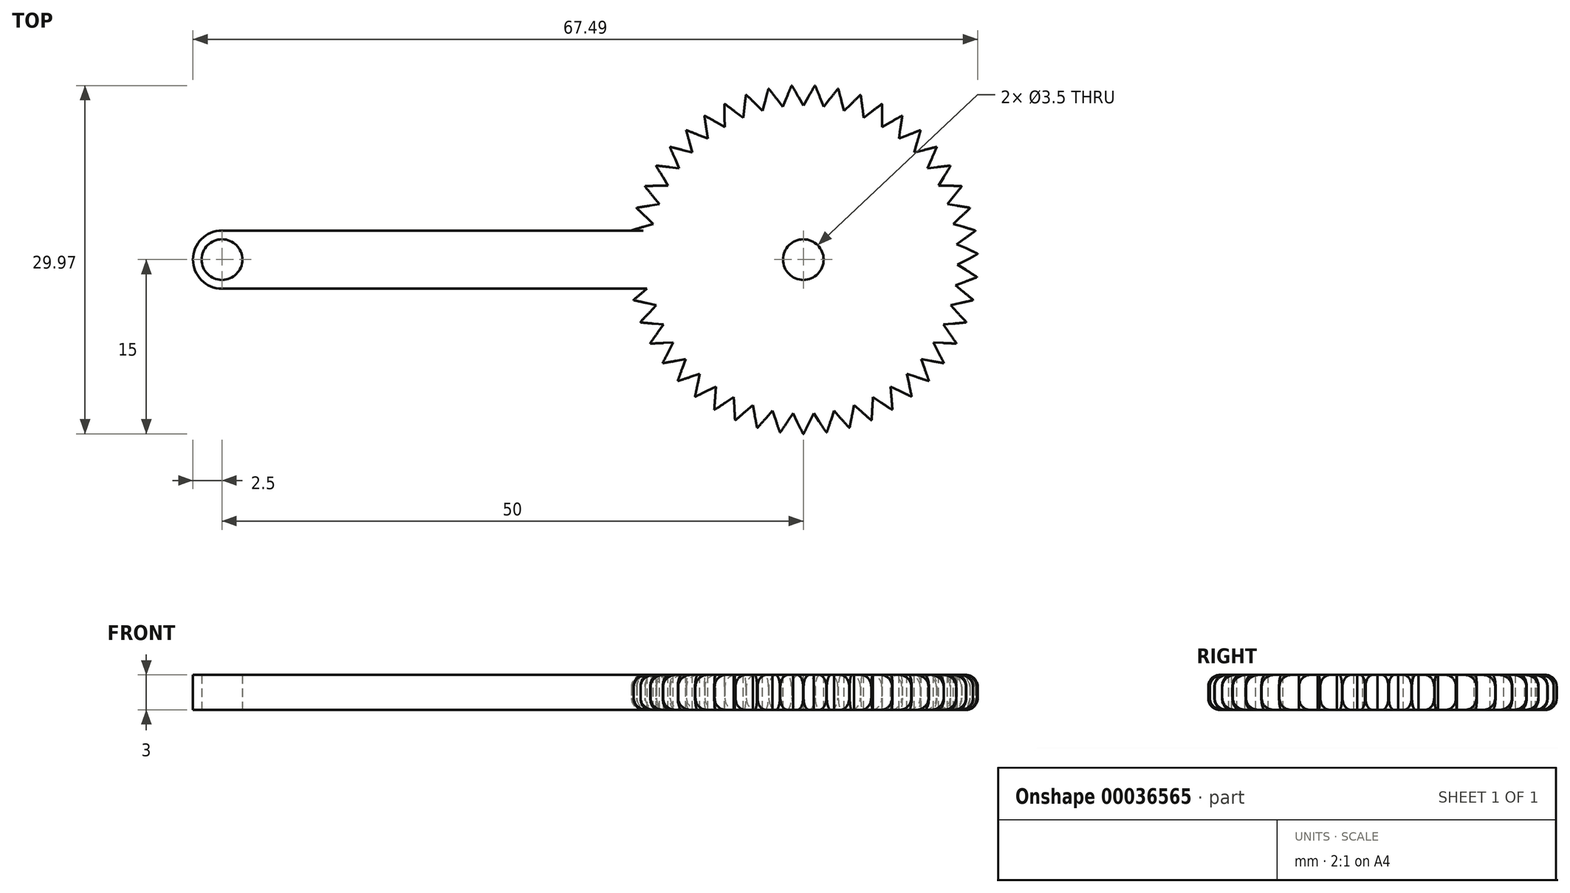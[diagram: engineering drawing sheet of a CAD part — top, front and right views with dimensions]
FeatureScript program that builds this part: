
annotation { "Feature Type Name" : "Feature", "Feature Type Description" : "" }
export const myFeature = defineFeature(function(context is Context, id is Id, definition is map)
    precondition{}
    {
        {
            var Q0;
            Q0=qCreatedBy(makeId("Top.planeOp"),FACE);
            var sketch = newSketch(context, id + "F0", { "sketchPlane" : qUnion([Q0])});
            skCircle(sketch, "E0", {"center": v(0, 0) * mm, "radius": 15 * mm});
            skSolve(sketch);
        }
        {
            var Q0;
            Q0 = qSketchRegion(id + "F0", true);
            extrude(context, id + "F1", {"entities" : qUnion([Q0]), "depth" : 3 * mm});
        }
        {
            var Q0;
            Q0=makeQuery(id+"F1.opExtrude","CAP_FACE",FACE,{"disambiguationData":[OSD([sQuery(id+"F0.wireOp",EDGE,"E0")])],"isStart":false});
            var Q1;
            Q1=makeQuery(id+"F1.opExtrude","CAP_EDGE",EDGE,{"disambiguationData":[OSD([sQuery(id+"F0.wireOp",EDGE,"E0")])],"isStart":true});
            fillet(context, id + "F2", {"entities" : qUnion([Q0, Q1]), "radius" : 1 * mm, "tangentPropagation" : true, "allowEdgeOverflow" : false});
        }
        {
            var Q0;
            Q0=makeQuery(id+"F1.opExtrude","CAP_FACE",FACE,{"disambiguationData":[OSD([sQuery(id+"F0.wireOp",EDGE,"E0")])],"isStart":false});
            var sketch = newSketch(context, id + "F3", { "sketchPlane" : qUnion([Q0])});
            skCircle(sketch, "E1.cCircle", {"center": v(0, 14.42) * mm, "radius": 0.58 * mm, "construction": true});
            skLineSegment(sketch, "E1.0", {"start": v(-1, 15) * mm, "end": v(1, 15) * mm});
            skLineSegment(sketch, "E1.1", {"start": v(1, 15) * mm, "end": v(0, 13.27) * mm});
            skLineSegment(sketch, "E1.2", {"start": v(0, 13.27) * mm, "end": v(-1, 15) * mm});
            skPoint(sketch, "E1.0.midPoint", {"position": v(0, 15) * mm});
            skLineSegment(sketch, "E2.1.0", {"start": v(-1, 15) * mm, "end": v(-1.77, 13.15) * mm});
            skLineSegment(sketch, "E2.1.1", {"start": v(-1.77, 13.15) * mm, "end": v(-3, 14.73) * mm});
            skLineSegment(sketch, "E2.1.2", {"start": v(-3, 14.73) * mm, "end": v(-1, 15) * mm});
            skLineSegment(sketch, "E2.2.0", {"start": v(-3, 14.73) * mm, "end": v(-3.5, 12.8) * mm});
            skLineSegment(sketch, "E2.2.1", {"start": v(-3.5, 12.8) * mm, "end": v(-4.93, 14.2) * mm});
            skLineSegment(sketch, "E2.2.2", {"start": v(-4.93, 14.2) * mm, "end": v(-3, 14.73) * mm});
            skLineSegment(sketch, "E2.3.0", {"start": v(-4.94, 14.2) * mm, "end": v(-5.18, 12.22) * mm});
            skLineSegment(sketch, "E2.3.1", {"start": v(-5.18, 12.22) * mm, "end": v(-6.78, 13.42) * mm});
            skLineSegment(sketch, "E2.3.2", {"start": v(-6.78, 13.42) * mm, "end": v(-4.94, 14.2) * mm});
            skLineSegment(sketch, "E2.4.0", {"start": v(-6.78, 13.42) * mm, "end": v(-6.76, 11.42) * mm});
            skLineSegment(sketch, "E2.4.1", {"start": v(-6.76, 11.42) * mm, "end": v(-8.5, 12.4) * mm});
            skLineSegment(sketch, "E2.4.2", {"start": v(-8.5, 12.4) * mm, "end": v(-6.78, 13.42) * mm});
            skLineSegment(sketch, "E2.5.0", {"start": v(-8.51, 12.4) * mm, "end": v(-8.22, 10.41) * mm});
            skLineSegment(sketch, "E2.5.1", {"start": v(-8.22, 10.41) * mm, "end": v(-10.08, 11.15) * mm});
            skLineSegment(sketch, "E2.5.2", {"start": v(-10.08, 11.15) * mm, "end": v(-8.51, 12.4) * mm});
            skLineSegment(sketch, "E2.6.0", {"start": v(-10.09, 11.15) * mm, "end": v(-9.54, 9.22) * mm});
            skLineSegment(sketch, "E2.6.1", {"start": v(-9.54, 9.22) * mm, "end": v(-11.48, 9.7) * mm});
            skLineSegment(sketch, "E2.6.2", {"start": v(-11.48, 9.7) * mm, "end": v(-10.09, 11.15) * mm});
            skLineSegment(sketch, "E2.7.0", {"start": v(-11.48, 9.7) * mm, "end": v(-10.68, 7.87) * mm});
            skLineSegment(sketch, "E2.7.1", {"start": v(-10.68, 7.87) * mm, "end": v(-12.67, 8.1) * mm});
            skLineSegment(sketch, "E2.7.2", {"start": v(-12.67, 8.1) * mm, "end": v(-11.48, 9.7) * mm});
            skLineSegment(sketch, "E2.8.0", {"start": v(-12.67, 8.09) * mm, "end": v(-11.64, 6.38) * mm});
            skLineSegment(sketch, "E2.8.1", {"start": v(-11.64, 6.38) * mm, "end": v(-13.63, 6.33) * mm});
            skLineSegment(sketch, "E2.8.2", {"start": v(-13.63, 6.33) * mm, "end": v(-12.67, 8.09) * mm});
            skLineSegment(sketch, "E2.9.0", {"start": v(-13.64, 6.32) * mm, "end": v(-12.38, 4.77) * mm});
            skLineSegment(sketch, "E2.9.1", {"start": v(-12.38, 4.77) * mm, "end": v(-14.36, 4.46) * mm});
            skLineSegment(sketch, "E2.9.2", {"start": v(-14.36, 4.46) * mm, "end": v(-13.64, 6.32) * mm});
            skLineSegment(sketch, "E2.10.0", {"start": v(-14.36, 4.45) * mm, "end": v(-12.9, 3.08) * mm});
            skLineSegment(sketch, "E2.10.1", {"start": v(-12.9, 3.08) * mm, "end": v(-14.82, 2.5) * mm});
            skLineSegment(sketch, "E2.10.2", {"start": v(-14.82, 2.5) * mm, "end": v(-14.36, 4.45) * mm});
            skLineSegment(sketch, "E2.11.0", {"start": v(-14.82, 2.5) * mm, "end": v(-13.2, 1.33) * mm});
            skLineSegment(sketch, "E2.11.1", {"start": v(-13.2, 1.33) * mm, "end": v(-15.02, 0.5) * mm});
            skLineSegment(sketch, "E2.11.2", {"start": v(-15.02, 0.5) * mm, "end": v(-14.82, 2.5) * mm});
            skLineSegment(sketch, "E2.12.0", {"start": v(-15.03, 0.5) * mm, "end": v(-13.26, -0.44) * mm});
            skLineSegment(sketch, "E2.12.1", {"start": v(-13.26, -0.44) * mm, "end": v(-14.96, -1.5) * mm});
            skLineSegment(sketch, "E2.12.2", {"start": v(-14.96, -1.5) * mm, "end": v(-15.03, 0.5) * mm});
            skLineSegment(sketch, "E2.13.0", {"start": v(-14.96, -1.5) * mm, "end": v(-13.08, -2.2) * mm});
            skLineSegment(sketch, "E2.13.1", {"start": v(-13.08, -2.2) * mm, "end": v(-14.62, -3.48) * mm});
            skLineSegment(sketch, "E2.13.2", {"start": v(-14.62, -3.48) * mm, "end": v(-14.96, -1.5) * mm});
            skLineSegment(sketch, "E2.14.0", {"start": v(-14.62, -3.49) * mm, "end": v(-12.67, -3.93) * mm});
            skLineSegment(sketch, "E2.14.1", {"start": v(-12.67, -3.93) * mm, "end": v(-14.03, -5.4) * mm});
            skLineSegment(sketch, "E2.14.2", {"start": v(-14.03, -5.4) * mm, "end": v(-14.62, -3.49) * mm});
            skLineSegment(sketch, "E2.15.0", {"start": v(-14.03, -5.4) * mm, "end": v(-12.04, -5.58) * mm});
            skLineSegment(sketch, "E2.15.1", {"start": v(-12.04, -5.58) * mm, "end": v(-13.19, -7.22) * mm});
            skLineSegment(sketch, "E2.15.2", {"start": v(-13.19, -7.22) * mm, "end": v(-14.03, -5.4) * mm});
            skLineSegment(sketch, "E2.16.0", {"start": v(-13.18, -7.23) * mm, "end": v(-11.18, -7.14) * mm});
            skLineSegment(sketch, "E2.16.1", {"start": v(-11.18, -7.14) * mm, "end": v(-12.1, -8.91) * mm});
            skLineSegment(sketch, "E2.16.2", {"start": v(-12.1, -8.91) * mm, "end": v(-13.18, -7.23) * mm});
            skLineSegment(sketch, "E2.17.0", {"start": v(-12.1, -8.92) * mm, "end": v(-10.13, -8.57) * mm});
            skLineSegment(sketch, "E2.17.1", {"start": v(-10.13, -8.57) * mm, "end": v(-10.8, -10.45) * mm});
            skLineSegment(sketch, "E2.17.2", {"start": v(-10.8, -10.45) * mm, "end": v(-12.1, -8.92) * mm});
            skLineSegment(sketch, "E2.18.0", {"start": v(-10.8, -10.45) * mm, "end": v(-8.9, -9.84) * mm});
            skLineSegment(sketch, "E2.18.1", {"start": v(-8.9, -9.84) * mm, "end": v(-9.32, -11.8) * mm});
            skLineSegment(sketch, "E2.18.2", {"start": v(-9.32, -11.8) * mm, "end": v(-10.8, -10.45) * mm});
            skLineSegment(sketch, "E2.19.0", {"start": v(-9.31, -11.8) * mm, "end": v(-7.5, -10.94) * mm});
            skLineSegment(sketch, "E2.19.1", {"start": v(-7.5, -10.94) * mm, "end": v(-7.66, -12.93) * mm});
            skLineSegment(sketch, "E2.19.2", {"start": v(-7.66, -12.93) * mm, "end": v(-9.31, -11.8) * mm});
            skLineSegment(sketch, "E2.20.0", {"start": v(-7.66, -12.94) * mm, "end": v(-5.98, -11.84) * mm});
            skLineSegment(sketch, "E2.20.1", {"start": v(-5.98, -11.84) * mm, "end": v(-5.87, -13.84) * mm});
            skLineSegment(sketch, "E2.20.2", {"start": v(-5.87, -13.84) * mm, "end": v(-7.66, -12.94) * mm});
            skLineSegment(sketch, "E2.21.0", {"start": v(-5.87, -13.84) * mm, "end": v(-4.35, -12.53) * mm});
            skLineSegment(sketch, "E2.21.1", {"start": v(-4.35, -12.53) * mm, "end": v(-3.98, -14.5) * mm});
            skLineSegment(sketch, "E2.21.2", {"start": v(-3.98, -14.5) * mm, "end": v(-5.87, -13.84) * mm});
            skLineSegment(sketch, "E2.22.0", {"start": v(-3.97, -14.5) * mm, "end": v(-2.64, -13) * mm});
            skLineSegment(sketch, "E2.22.1", {"start": v(-2.64, -13) * mm, "end": v(-2, -14.9) * mm});
            skLineSegment(sketch, "E2.22.2", {"start": v(-2, -14.9) * mm, "end": v(-3.97, -14.5) * mm});
            skLineSegment(sketch, "E2.23.0", {"start": v(-2, -14.9) * mm, "end": v(-0.89, -13.24) * mm});
            skLineSegment(sketch, "E2.23.1", {"start": v(-0.89, -13.24) * mm, "end": v(0, -15.03) * mm});
            skLineSegment(sketch, "E2.23.2", {"start": v(0, -15.03) * mm, "end": v(-2, -14.9) * mm});
            skLineSegment(sketch, "E2.24.0", {"start": v(0, -15.03) * mm, "end": v(0.89, -13.24) * mm});
            skLineSegment(sketch, "E2.24.1", {"start": v(0.89, -13.24) * mm, "end": v(2, -14.9) * mm});
            skLineSegment(sketch, "E2.24.2", {"start": v(2, -14.9) * mm, "end": v(0, -15.03) * mm});
            skLineSegment(sketch, "E2.25.0", {"start": v(2, -14.9) * mm, "end": v(2.64, -13) * mm});
            skLineSegment(sketch, "E2.25.1", {"start": v(2.64, -13) * mm, "end": v(3.97, -14.5) * mm});
            skLineSegment(sketch, "E2.25.2", {"start": v(3.97, -14.5) * mm, "end": v(2, -14.9) * mm});
            skLineSegment(sketch, "E2.26.0", {"start": v(3.98, -14.5) * mm, "end": v(4.35, -12.53) * mm});
            skLineSegment(sketch, "E2.26.1", {"start": v(4.35, -12.53) * mm, "end": v(5.87, -13.84) * mm});
            skLineSegment(sketch, "E2.26.2", {"start": v(5.87, -13.84) * mm, "end": v(3.98, -14.5) * mm});
            skLineSegment(sketch, "E2.27.0", {"start": v(5.87, -13.84) * mm, "end": v(5.98, -11.84) * mm});
            skLineSegment(sketch, "E2.27.1", {"start": v(5.98, -11.84) * mm, "end": v(7.66, -12.94) * mm});
            skLineSegment(sketch, "E2.27.2", {"start": v(7.66, -12.94) * mm, "end": v(5.87, -13.84) * mm});
            skLineSegment(sketch, "E2.28.0", {"start": v(7.66, -12.93) * mm, "end": v(7.5, -10.94) * mm});
            skLineSegment(sketch, "E2.28.1", {"start": v(7.5, -10.94) * mm, "end": v(9.31, -11.8) * mm});
            skLineSegment(sketch, "E2.28.2", {"start": v(9.31, -11.8) * mm, "end": v(7.66, -12.93) * mm});
            skLineSegment(sketch, "E2.29.0", {"start": v(9.32, -11.8) * mm, "end": v(8.9, -9.84) * mm});
            skLineSegment(sketch, "E2.29.1", {"start": v(8.9, -9.84) * mm, "end": v(10.8, -10.45) * mm});
            skLineSegment(sketch, "E2.29.2", {"start": v(10.8, -10.45) * mm, "end": v(9.32, -11.8) * mm});
            skLineSegment(sketch, "E2.30.0", {"start": v(10.8, -10.45) * mm, "end": v(10.13, -8.57) * mm});
            skLineSegment(sketch, "E2.30.1", {"start": v(10.13, -8.57) * mm, "end": v(12.1, -8.92) * mm});
            skLineSegment(sketch, "E2.30.2", {"start": v(12.1, -8.92) * mm, "end": v(10.8, -10.45) * mm});
            skLineSegment(sketch, "E2.31.0", {"start": v(12.1, -8.91) * mm, "end": v(11.18, -7.14) * mm});
            skLineSegment(sketch, "E2.31.1", {"start": v(11.18, -7.14) * mm, "end": v(13.18, -7.23) * mm});
            skLineSegment(sketch, "E2.31.2", {"start": v(13.18, -7.23) * mm, "end": v(12.1, -8.91) * mm});
            skLineSegment(sketch, "E2.32.0", {"start": v(13.19, -7.22) * mm, "end": v(12.04, -5.58) * mm});
            skLineSegment(sketch, "E2.32.1", {"start": v(12.04, -5.58) * mm, "end": v(14.03, -5.4) * mm});
            skLineSegment(sketch, "E2.32.2", {"start": v(14.03, -5.4) * mm, "end": v(13.19, -7.22) * mm});
            skLineSegment(sketch, "E2.33.0", {"start": v(14.03, -5.4) * mm, "end": v(12.67, -3.93) * mm});
            skLineSegment(sketch, "E2.33.1", {"start": v(12.67, -3.93) * mm, "end": v(14.62, -3.49) * mm});
            skLineSegment(sketch, "E2.33.2", {"start": v(14.62, -3.49) * mm, "end": v(14.03, -5.4) * mm});
            skLineSegment(sketch, "E2.34.0", {"start": v(14.62, -3.48) * mm, "end": v(13.08, -2.2) * mm});
            skLineSegment(sketch, "E2.34.1", {"start": v(13.08, -2.2) * mm, "end": v(14.96, -1.5) * mm});
            skLineSegment(sketch, "E2.34.2", {"start": v(14.96, -1.5) * mm, "end": v(14.62, -3.48) * mm});
            skLineSegment(sketch, "E2.35.0", {"start": v(14.96, -1.5) * mm, "end": v(13.26, -0.44) * mm});
            skLineSegment(sketch, "E2.35.1", {"start": v(13.26, -0.44) * mm, "end": v(15.03, 0.5) * mm});
            skLineSegment(sketch, "E2.35.2", {"start": v(15.03, 0.5) * mm, "end": v(14.96, -1.5) * mm});
            skLineSegment(sketch, "E2.36.0", {"start": v(15.02, 0.5) * mm, "end": v(13.2, 1.33) * mm});
            skLineSegment(sketch, "E2.36.1", {"start": v(13.2, 1.33) * mm, "end": v(14.82, 2.5) * mm});
            skLineSegment(sketch, "E2.36.2", {"start": v(14.82, 2.5) * mm, "end": v(15.02, 0.5) * mm});
            skLineSegment(sketch, "E2.37.0", {"start": v(14.82, 2.5) * mm, "end": v(12.9, 3.08) * mm});
            skLineSegment(sketch, "E2.37.1", {"start": v(12.9, 3.08) * mm, "end": v(14.36, 4.45) * mm});
            skLineSegment(sketch, "E2.37.2", {"start": v(14.36, 4.45) * mm, "end": v(14.82, 2.5) * mm});
            skLineSegment(sketch, "E2.38.0", {"start": v(14.36, 4.46) * mm, "end": v(12.38, 4.77) * mm});
            skLineSegment(sketch, "E2.38.1", {"start": v(12.38, 4.77) * mm, "end": v(13.64, 6.32) * mm});
            skLineSegment(sketch, "E2.38.2", {"start": v(13.64, 6.32) * mm, "end": v(14.36, 4.46) * mm});
            skLineSegment(sketch, "E2.39.0", {"start": v(13.63, 6.33) * mm, "end": v(11.64, 6.38) * mm});
            skLineSegment(sketch, "E2.39.1", {"start": v(11.64, 6.38) * mm, "end": v(12.67, 8.09) * mm});
            skLineSegment(sketch, "E2.39.2", {"start": v(12.67, 8.09) * mm, "end": v(13.63, 6.33) * mm});
            skLineSegment(sketch, "E2.40.0", {"start": v(12.67, 8.1) * mm, "end": v(10.68, 7.87) * mm});
            skLineSegment(sketch, "E2.40.1", {"start": v(10.68, 7.87) * mm, "end": v(11.48, 9.7) * mm});
            skLineSegment(sketch, "E2.40.2", {"start": v(11.48, 9.7) * mm, "end": v(12.67, 8.1) * mm});
            skLineSegment(sketch, "E2.41.0", {"start": v(11.48, 9.7) * mm, "end": v(9.54, 9.22) * mm});
            skLineSegment(sketch, "E2.41.1", {"start": v(9.54, 9.22) * mm, "end": v(10.09, 11.15) * mm});
            skLineSegment(sketch, "E2.41.2", {"start": v(10.09, 11.15) * mm, "end": v(11.48, 9.7) * mm});
            skLineSegment(sketch, "E2.42.0", {"start": v(10.08, 11.15) * mm, "end": v(8.22, 10.41) * mm});
            skLineSegment(sketch, "E2.42.1", {"start": v(8.22, 10.41) * mm, "end": v(8.51, 12.4) * mm});
            skLineSegment(sketch, "E2.42.2", {"start": v(8.51, 12.4) * mm, "end": v(10.08, 11.15) * mm});
            skLineSegment(sketch, "E2.43.0", {"start": v(8.5, 12.4) * mm, "end": v(6.76, 11.42) * mm});
            skLineSegment(sketch, "E2.43.1", {"start": v(6.76, 11.42) * mm, "end": v(6.78, 13.42) * mm});
            skLineSegment(sketch, "E2.43.2", {"start": v(6.78, 13.42) * mm, "end": v(8.5, 12.4) * mm});
            skLineSegment(sketch, "E2.44.0", {"start": v(6.78, 13.42) * mm, "end": v(5.18, 12.22) * mm});
            skLineSegment(sketch, "E2.44.1", {"start": v(5.18, 12.22) * mm, "end": v(4.94, 14.2) * mm});
            skLineSegment(sketch, "E2.44.2", {"start": v(4.94, 14.2) * mm, "end": v(6.78, 13.42) * mm});
            skLineSegment(sketch, "E2.45.0", {"start": v(4.93, 14.2) * mm, "end": v(3.5, 12.8) * mm});
            skLineSegment(sketch, "E2.45.1", {"start": v(3.5, 12.8) * mm, "end": v(3, 14.73) * mm});
            skLineSegment(sketch, "E2.45.2", {"start": v(3, 14.73) * mm, "end": v(4.93, 14.2) * mm});
            skLineSegment(sketch, "E2.46.0", {"start": v(3, 14.73) * mm, "end": v(1.77, 13.15) * mm});
            skLineSegment(sketch, "E2.46.1", {"start": v(1.77, 13.15) * mm, "end": v(1, 15) * mm});
            skLineSegment(sketch, "E2.46.2", {"start": v(1, 15) * mm, "end": v(3, 14.73) * mm});
            skPoint(sketch, "E2.center", {"position": v(0, 0) * mm});
            skSolve(sketch);
        }
        {
            var Q0;
            Q0 = qSketchRegion(id + "F3", true);
            extrude(context, id + "F4", {"entities" : qUnion([Q0]), "operationType" : NewBodyOperationType.REMOVE, "endBound" : BoundingType.THROUGH_ALL, "oppositeDirection" : true, "depth" : 25 * mm});
        }
        {
            var Q0;
            Q0=qCreatedBy(makeId("Top.planeOp"),FACE);
            var sketch = newSketch(context, id + "F5", { "sketchPlane" : qUnion([Q0])});
            skLineSegment(sketch, "E3.bottom", {"start": v(-50, 2.5) * mm, "end": v(0, 2.5) * mm});
            skLineSegment(sketch, "E3.top", {"start": v(-50, -2.5) * mm, "end": v(0, -2.5) * mm});
            skLineSegment(sketch, "E3.right", {"start": v(0, 2.5) * mm, "end": v(0, -2.5) * mm});
            skArc(sketch, "E4", {"start": v(-50, 2.5) * mm, "mid": v(-52.5, 0) * mm, "end": v(-50, -2.5) * mm});
            skCircle(sketch, "E5", {"center": v(-50, 0) * mm, "radius": 1.75 * mm});
            skSolve(sketch);
        }
        {
            var Q0;
            Q0 = qSketchRegion(id + "F5", true);
            extrude(context, id + "F6", {"entities" : qUnion([Q0]), "operationType" : NewBodyOperationType.ADD, "depth" : 3 * mm});
        }
        {
            var Q0;
            Q0=makeQuery(id+"F6.boolean.opBoolean","MERGE",FACE,{"derivedFrom":[makeQuery(id+"F1.opExtrude","CAP_FACE",FACE,{"disambiguationData":[OSD([sQuery(id+"F0.wireOp",EDGE,"E0")])],"isStart":false}),makeQuery(id+"F6.opExtrude","CAP_FACE",FACE,{"disambiguationData":[OSD([sQuery(id+"F5.wireOp",EDGE,"E3.bottom"),sQuery(id+"F5.wireOp",EDGE,"E3.top"),sQuery(id+"F5.wireOp",EDGE,"E3.right"),sQuery(id+"F5.wireOp",EDGE,"E4"),sQuery(id+"F5.wireOp",EDGE,"E5")])],"isStart":false})]});
            var sketch = newSketch(context, id + "F7", { "sketchPlane" : qUnion([Q0])});
            skCircle(sketch, "E6", {"center": v(0, 0) * mm, "radius": 1.75 * mm});
            skSolve(sketch);
        }
        {
            var Q0;
            Q0 = qSketchRegion(id + "F7", true);
            extrude(context, id + "F8", {"entities" : qUnion([Q0]), "operationType" : NewBodyOperationType.REMOVE, "endBound" : BoundingType.THROUGH_ALL, "oppositeDirection" : true, "depth" : 25 * mm});
        }
    });
